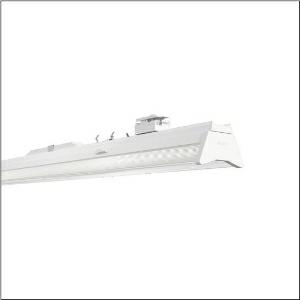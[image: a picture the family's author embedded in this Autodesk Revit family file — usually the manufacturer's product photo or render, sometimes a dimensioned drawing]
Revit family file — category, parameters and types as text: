
# Revit family: licross_21_performance_mo_52td16dn445g
name_source: partatom
category: Lighting Fixtures
units: mm (PartAtom-declared; Revit-internal decimal feet)

## family parameters
Cut with Voids When Loaded = No
Host = Face
Light Source = No
Part Type = Normal
Room Calculation Point = No
Round Connector Dimension = Use Diameter
Shared = No

## types (1)
- --- (1 x LED, 4500 lm, 24.9 W, 4000K)
    Apparent Load = 25 VA
    CIE Flux Codes = 66 88 96 79 100
    Color Rendering = 80
    Color Temperature = 4000K
    Default Elevation = 1800 mm
    Description = Licross 21 Performance MO, luminaire insert, of sheet steel, galvanised, coil coated, white, length: 1.500mm, width: 120mm, height: 123mm, LED rated luminous flux: 4.500lm, light colour: 840, SDCM (Standard Deviation of Colour Matching)MacAdam ≤ 3 SDCM (initial), control gear: DALI 2, with plug, 5-pole, with phase selection, mains connection: 220..240V, AC, 50/60Hz, rated input power: 25W, internal wiring halogen-free, primary light control with lens, of plastic, primary optical cover: cover, of PMMA, CAT 2 (L<= 3000cd/m²), light emission: direct/indirect distribution, primary light characteristic: symmetric, protection rating (complete): IP54, insulation class (complete): insulation class I (protective earthing), certification: CE, ENEC, VDE, UKCA, protection symbol: D if used in an environment with non-conductive dust loads with corresponding accessories, impact resistance: IK06, permissible ambient temperature for indoor applications: -25..+50°C, corresponds to IFS (International Featured Standards) requirements for safety and quality in the food industry, reducing of maximum allowable ambient temperature of 5°C with ceiling mounting, LABS conformity tested according to VDMA 24364:2018-05, The light source and the operating device comply with the requirements of the Ecodesign Regulation (EU) 2019/2020 and are replaceable in accordance with this regulation, packaging unit: 1 piece
    Height = 114 mm
    Lamp = 1 x LED
    Lamp Light Flux = 4500 lm
    Lamp Power = 24.9 W
    Lamp count = 1
    Length = 1500 mm
    Luminous efficacy = 181 lm/W
    Manufacturer = Siteco
    ModVariant = No
    Model = 52TD16DN445G
    Mounting Place = Ceiling
    Mounting Type = Pendant
    Number of Poles = 1
    OnlyDefault = Yes
    Power Factor = 1
    Product Name = Licross 21 Performance MO
    Product group = luminaire insert | ceiling pendant
    ProductGroupID = 901
    Protection Class = Protection class I
    Protection Degree = IP 54
    RLX_Detail_Level = 1
    RLX_Emergency_Light_Flux = 0 lm
    RLX_Emergency_Type = 0
    RLX_Emergency_Type_DB = No
    RlxData = <blob elided: 33869 chars, md5=69e5e7b9>
    Socket = socket
    Standby Power = 0 W
    System Light Flux = 4500 lm
    System Power = 25 W
    Type Comments = factory setting: luminous flux: 100 % | dim-lin: 254 | 165 mA
    Type Image = l_1256138.jpg
    URL = http://relux.com
    VarID = @adj_056225
    Voltage = 0 V
    Weight = 0.00 kg
    Width = 120 mm

## geometry (parser evidence)
native form markers: Blend x4, Sweep x12
no freeform markers — native parametric forms only
